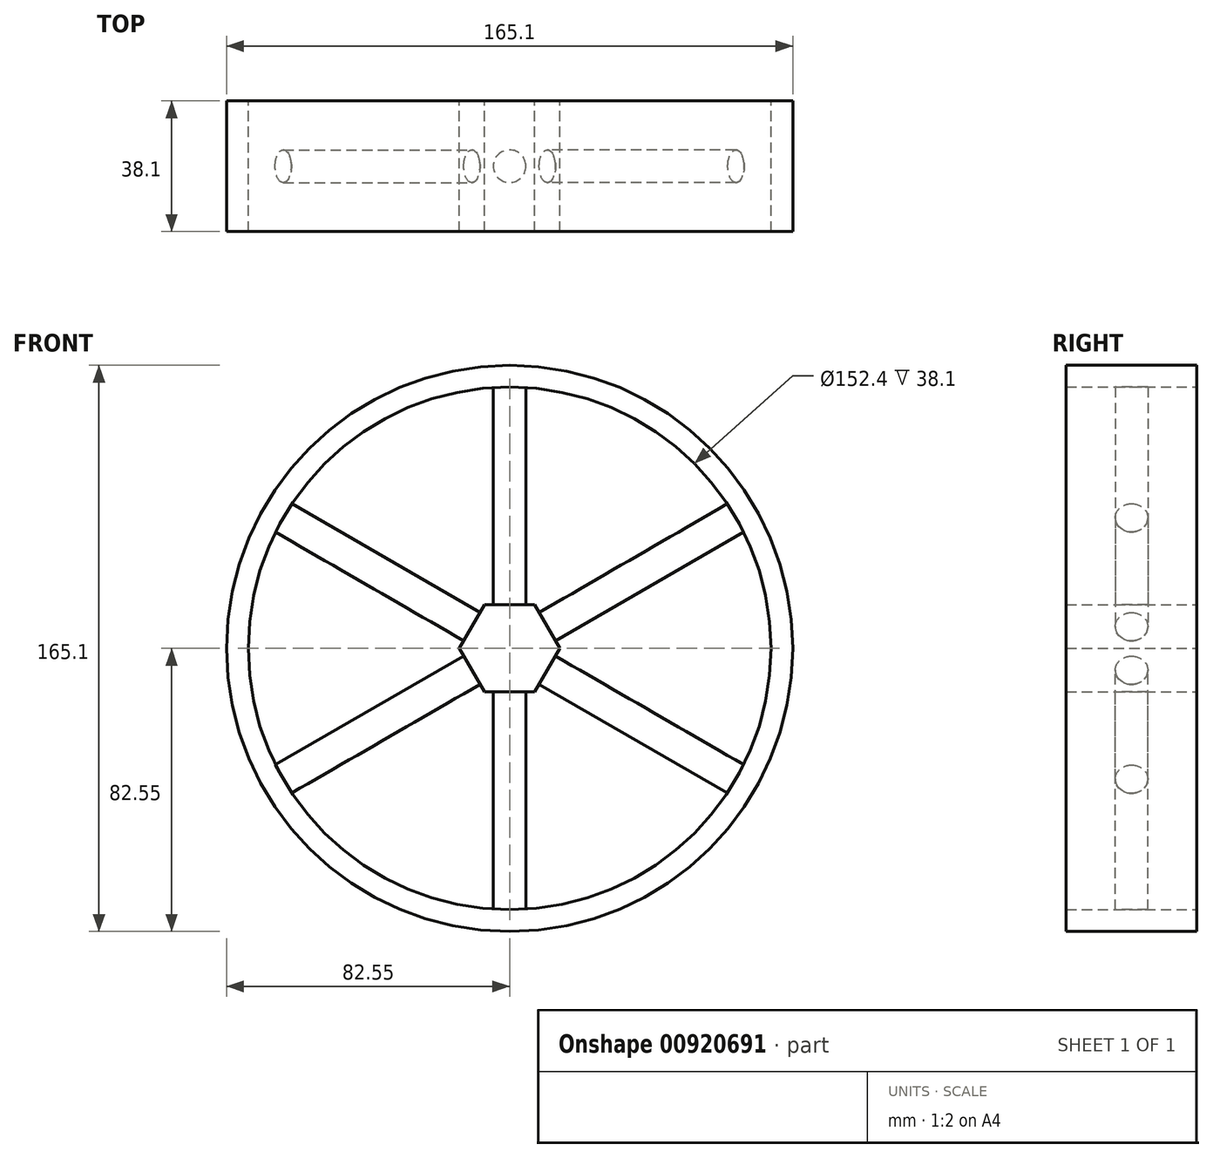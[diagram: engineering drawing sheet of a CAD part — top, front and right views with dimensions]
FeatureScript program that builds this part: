
annotation { "Feature Type Name" : "Feature", "Feature Type Description" : "" }
export const myFeature = defineFeature(function(context is Context, id is Id, definition is map)
    precondition{}
    {
        {
            var Q0;
            Q0=qCreatedBy(makeId("Front.planeOp"),FACE);
            var sketch = newSketch(context, id + "F0", { "sketchPlane" : qUnion([Q0])});
            skCircle(sketch, "E0.cCircle", {"center": v(0, 0) * mm, "radius": 12.7 * mm, "construction": true});
            skLineSegment(sketch, "E0.0", {"start": v(7.33, 12.7) * mm, "end": v(14.66, 0) * mm});
            skLineSegment(sketch, "E0.1", {"start": v(14.66, 0) * mm, "end": v(7.33, -12.7) * mm});
            skLineSegment(sketch, "E0.2", {"start": v(7.33, -12.7) * mm, "end": v(-7.33, -12.7) * mm});
            skLineSegment(sketch, "E0.3", {"start": v(-7.33, -12.7) * mm, "end": v(-14.66, 0) * mm});
            skLineSegment(sketch, "E0.4", {"start": v(-14.66, 0) * mm, "end": v(-7.33, 12.7) * mm});
            skLineSegment(sketch, "E0.5", {"start": v(-7.33, 12.7) * mm, "end": v(7.33, 12.7) * mm});
            skPoint(sketch, "E0.0.midPoint", {"position": v(11, 6.35) * mm});
            skCircle(sketch, "E1", {"center": v(0, 0) * mm, "radius": 76.2 * mm});
            skCircle(sketch, "E2", {"center": v(0, 0) * mm, "radius": 82.55 * mm});
            skSolve(sketch);
        }
        {
            var Q0;
            Q0 = qSketchRegion(id + "F0", true);
            var Q1;
            Q1=makeQuery(id+"F0.imprint","IMPRINT",FACE,{"disambiguationData":[TD([[makeQuery(id+"F0.imprint","IMPRINT",EDGE,{"derivedFrom":sQuery(id+"F0.wireOp",EDGE,"E0.0")}),-1.0]])]});
            extrude(context, id + "F1", {"entities" : qUnion([Q0, Q1]), "depth" : 38.1 * mm, "offsetDistance" : 25.4 * mm});
        }
        {
            var Q0;
            Q0=makeQuery(id+"F1.opExtrude","CAP_FACE",FACE,{"disambiguationData":[OSD([sQuery(id+"F0.wireOp",EDGE,"E0.0"),sQuery(id+"F0.wireOp",EDGE,"E0.1"),sQuery(id+"F0.wireOp",EDGE,"E0.2"),sQuery(id+"F0.wireOp",EDGE,"E0.3"),sQuery(id+"F0.wireOp",EDGE,"E0.4"),sQuery(id+"F0.wireOp",EDGE,"E0.5")])],"isStart":false});
            var Q1;
            Q1=makeQuery(id+"F1.opExtrude","CAP_FACE",FACE,{"disambiguationData":[OSD([sQuery(id+"F0.wireOp",EDGE,"E0.0"),sQuery(id+"F0.wireOp",EDGE,"E0.1"),sQuery(id+"F0.wireOp",EDGE,"E0.2"),sQuery(id+"F0.wireOp",EDGE,"E0.3"),sQuery(id+"F0.wireOp",EDGE,"E0.4"),sQuery(id+"F0.wireOp",EDGE,"E0.5")])],"isStart":true});
            cPlane(context, id + "F2", {"entities" : qUnion([Q0, Q1]), "cplaneType" : CPlaneType.MID_PLANE, "offset" : 25.4 * mm, "width" : 152.4 * mm, "height" : 152.4 * mm});
        }
        {
            var Q0;
            Q0=qCreatedBy(id+"F2.planeOp",FACE);
            var sketch = newSketch(context, id + "F3", { "sketchPlane" : qUnion([Q0])});
            skLineSegment(sketch, "E3", {"start": v(0, 12.7) * mm, "end": v(0, 76.2) * mm});
            skLineSegment(sketch, "E4", {"start": v(0, 76.2) * mm, "end": v(0, 76.2) * mm});
            skLineSegment(sketch, "E5", {"start": v(0, 76.2) * mm, "end": v(4.76, 76.2) * mm});
            skLineSegment(sketch, "E6", {"start": v(4.76, 76.2) * mm, "end": v(4.76, 12.7) * mm});
            skLineSegment(sketch, "E7", {"start": v(4.76, 12.7) * mm, "end": v(0, 12.7) * mm});
            skSolve(sketch);
        }
        {
            var Q0;
            Q0=makeQuery(id+"F3.imprint","IMPRINT",FACE,{"disambiguationData":[TD([[makeQuery(id+"F3.imprint","IMPRINT",EDGE,{"derivedFrom":sQuery(id+"F3.wireOp",EDGE,"E3")}),-1.0]])]});
            var Q1;
            Q1=sQuery(id+"F3.wireOp",EDGE,"E3");
            revolve(context, id + "F4", {"surfaceOperationType" : NewSurfaceOperationType.NEW, "entities" : qUnion([Q0]), "axis" : qUnion([Q1]), "revolveType" : RevolveType.FULL});
        }
        {
            var Q0;
            Q0=makeQuery(id+"F4.opRevolve","SWEPT_BODY",BODY,{"disambiguationData":[OSD([sQuery(id+"F3.wireOp",EDGE,"E3"),sQuery(id+"F3.wireOp",EDGE,"E5"),sQuery(id+"F3.wireOp",EDGE,"E6"),sQuery(id+"F3.wireOp",EDGE,"E7")])]});
            var Q1;
            Q1=makeQuery(id+"F1.opExtrude","SWEPT_FACE",FACE,{"disambiguationData":[OSD([sQuery(id+"F0.wireOp",EDGE,"E2")])]});
            circularPattern(context, id + "F5", {"entities" : qUnion([Q0]), "axis" : qUnion([Q1]), "angle" : 360 * degree, "instanceCount" : 6, "equalSpace" : true});
        }
    });
